# Revit family: TBW08408B_TAC
name_source: partatom
category: 衛生器具
revit_build: Autodesk Revit 2018 (Build: 20190510_1515(x64)
units: mm (PartAtom-declared; Revit-internal decimal feet)

## family parameters
OmniClass タイトル = Sanitary, Laundry, and Cleaning Equipment
OmniClass 番号 = 23.45.00.00
パーツ タイプ = 標準
ロード時にボイドで切り取り = いいえ
丸型コネクタ寸法 = 直径を使用
作業面ベース = いいえ
共有 = いいえ
常に垂直 = はい
部屋計算ポイント = いいえ

## types (1)
- TBW08408B_TAC
    Finish = Polished Chrome
    Height = 1530  [stored 5.01969 ft]
    Length = 545  [stored 1.78806 ft]
    Material = <カテゴリ別>
    URL = https://asia.toto.com
    Water Pressure = 0.05~1.0MPa
    Width = 712  [stored 2.33596 ft]
    モデル = TBW08408B
    排気配管 = いいえ
    排水配管 = いいえ
    水配管 = はい
    温水配管 = はい
    製造元 = TOTO LTD.
    説明 = Thermostat Shower Column with Over Head Shower(2 mode)

note: [stored X ft] marks values corroborated as IEEE doubles in the binary element streams (Revit-internal decimal feet)

## geometry (parser evidence)
native form markers: Sweep x3
no freeform markers — native parametric forms only
